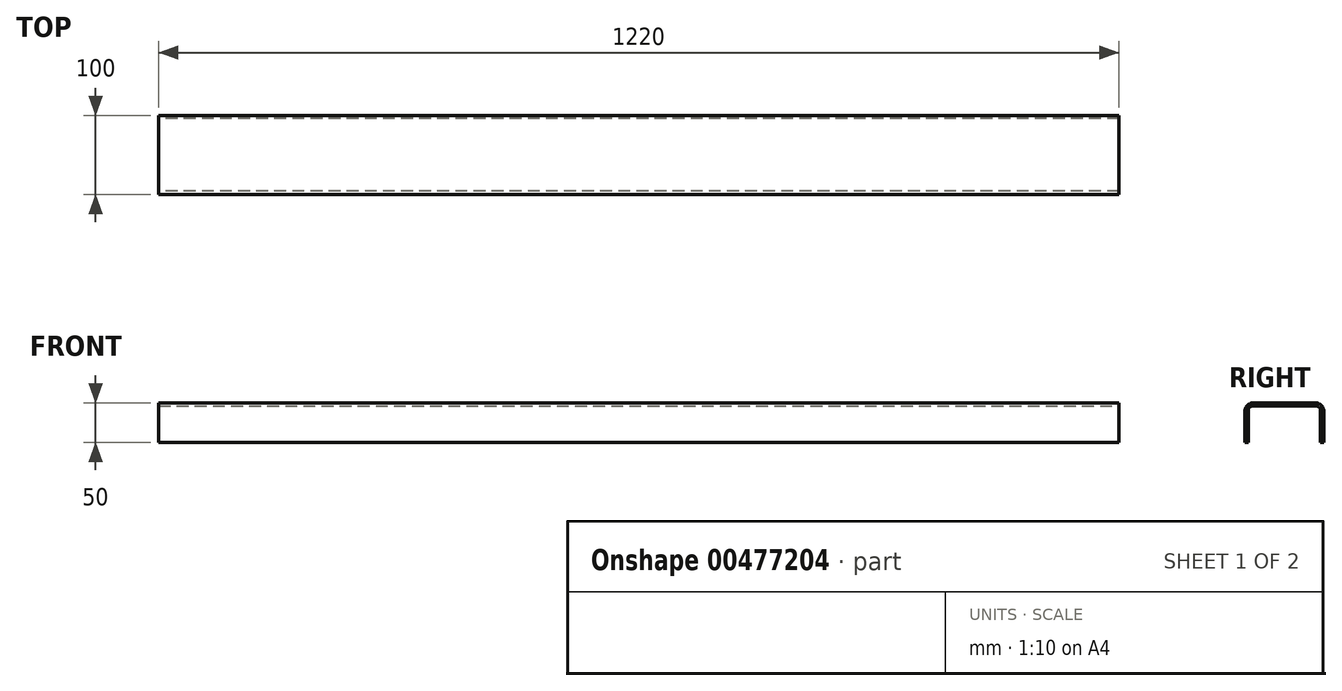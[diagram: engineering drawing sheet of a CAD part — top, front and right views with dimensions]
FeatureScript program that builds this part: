
annotation { "Feature Type Name" : "Feature", "Feature Type Description" : "" }
export const myFeature = defineFeature(function(context is Context, id is Id, definition is map)
    precondition{}
    {
        {
            var Q0;
            Q0=qCreatedBy(makeId("Right.planeOp"),FACE);
            var sketch = newSketch(context, id + "F0", { "sketchPlane" : qUnion([Q0])});
            skLineSegment(sketch, "E0.bottom", {"start": v(0, 0) * mm, "end": v(100, 0) * mm});
            skLineSegment(sketch, "E0.top", {"start": v(10, 50) * mm, "end": v(90, 50) * mm});
            skLineSegment(sketch, "E0.left", {"start": v(0, 0) * mm, "end": v(0, 40) * mm});
            skLineSegment(sketch, "E0.right", {"start": v(100, 0) * mm, "end": v(100, 40) * mm});
            skPoint(sketch, "E1.visualSharp", {"position": v(0, 50) * mm});
            skArc(sketch, "E1.filletArc", {"start": v(10, 50) * mm, "mid": v(2.93, 47.07) * mm, "end": v(0, 40) * mm});
            skPoint(sketch, "E2.visualSharp", {"position": v(100, 50) * mm});
            skArc(sketch, "E2.filletArc", {"start": v(100, 40) * mm, "mid": v(97.07, 47.07) * mm, "end": v(90, 50) * mm});
            skSolve(sketch);
        }
        {
            var Q0;
            Q0=makeQuery(id+"F0.imprint","IMPRINT",FACE,{"disambiguationData":[TD([[makeQuery(id+"F0.imprint","IMPRINT",EDGE,{"derivedFrom":sQuery(id+"F0.wireOp",EDGE,"E0.bottom")}),1.0]])]});
            extrude(context, id + "F1", {"entities" : qUnion([Q0]), "depth" : 1220 * mm});
        }
        {
            var Q0;
            Q0=makeQuery(id+"F1.opExtrude","SWEPT_FACE",FACE,{"disambiguationData":[OSD([sQuery(id+"F0.wireOp",EDGE,"E0.bottom")])]});
            var Q1;
            Q1=makeQuery(id+"F1.opExtrude","CAP_FACE",FACE,{"disambiguationData":[OSD([sQuery(id+"F0.wireOp",EDGE,"E0.bottom"),sQuery(id+"F0.wireOp",EDGE,"E0.top"),sQuery(id+"F0.wireOp",EDGE,"E0.left"),sQuery(id+"F0.wireOp",EDGE,"E0.right"),sQuery(id+"F0.wireOp",EDGE,"E1.filletArc"),sQuery(id+"F0.wireOp",EDGE,"E2.filletArc")])],"isStart":false});
            var Q2;
            Q2=makeQuery(id+"F1.opExtrude","CAP_FACE",FACE,{"disambiguationData":[OSD([sQuery(id+"F0.wireOp",EDGE,"E0.bottom"),sQuery(id+"F0.wireOp",EDGE,"E0.top"),sQuery(id+"F0.wireOp",EDGE,"E0.left"),sQuery(id+"F0.wireOp",EDGE,"E0.right"),sQuery(id+"F0.wireOp",EDGE,"E1.filletArc"),sQuery(id+"F0.wireOp",EDGE,"E2.filletArc")])],"isStart":true});
            shell(context, id + "F2", {"entities" : qUnion([Q0, Q1, Q2]), "thickness" : 4 * mm});
        }
    });
